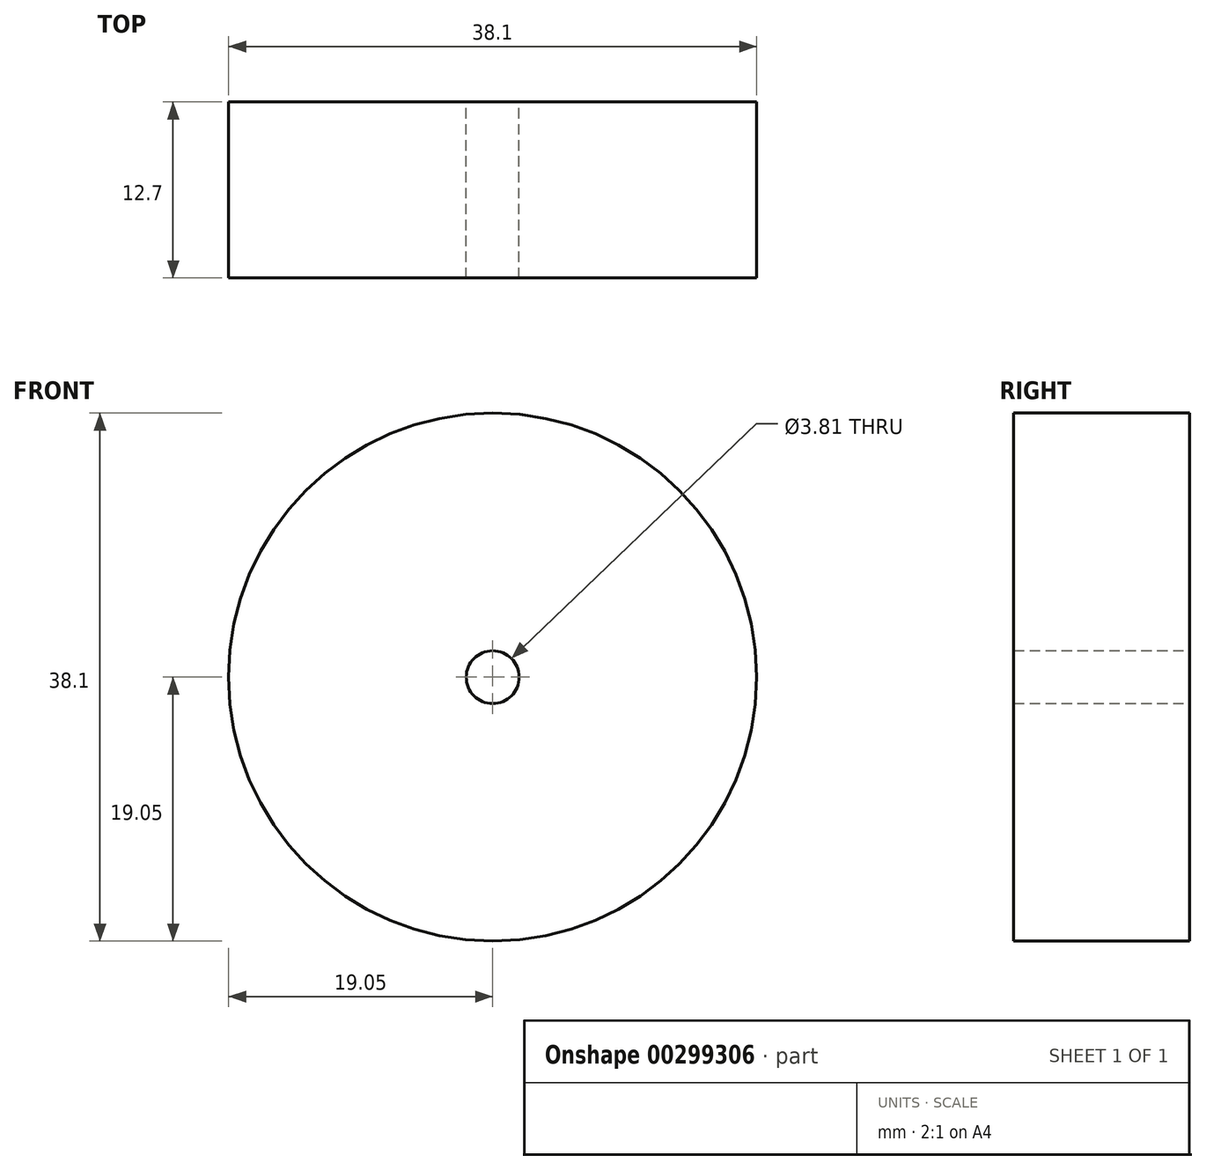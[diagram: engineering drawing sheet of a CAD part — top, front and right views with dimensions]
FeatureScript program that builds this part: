
annotation { "Feature Type Name" : "Feature", "Feature Type Description" : "" }
export const myFeature = defineFeature(function(context is Context, id is Id, definition is map)
    precondition{}
    {
        {
            var Q0;
            Q0=qCreatedBy(makeId("Front.planeOp"),FACE);
            var sketch = newSketch(context, id + "F0", { "sketchPlane" : qUnion([Q0])});
            skCircle(sketch, "E0", {"center": v(0, 0) * mm, "radius": 19.05 * mm});
            skCircle(sketch, "E1", {"center": v(0, 0) * mm, "radius": 1.9 * mm});
            skSolve(sketch);
        }
        {
            var Q0;
            Q0=makeQuery(id+"F0.imprint","IMPRINT",FACE,{"disambiguationData":[TD([[makeQuery(id+"F0.imprint","IMPRINT",EDGE,{"derivedFrom":sQuery(id+"F0.wireOp",EDGE,"E0")}),1.0]])]});
            extrude(context, id + "F1", {"entities" : qUnion([Q0]), "depth" : 12.7 * mm});
        }
    });
